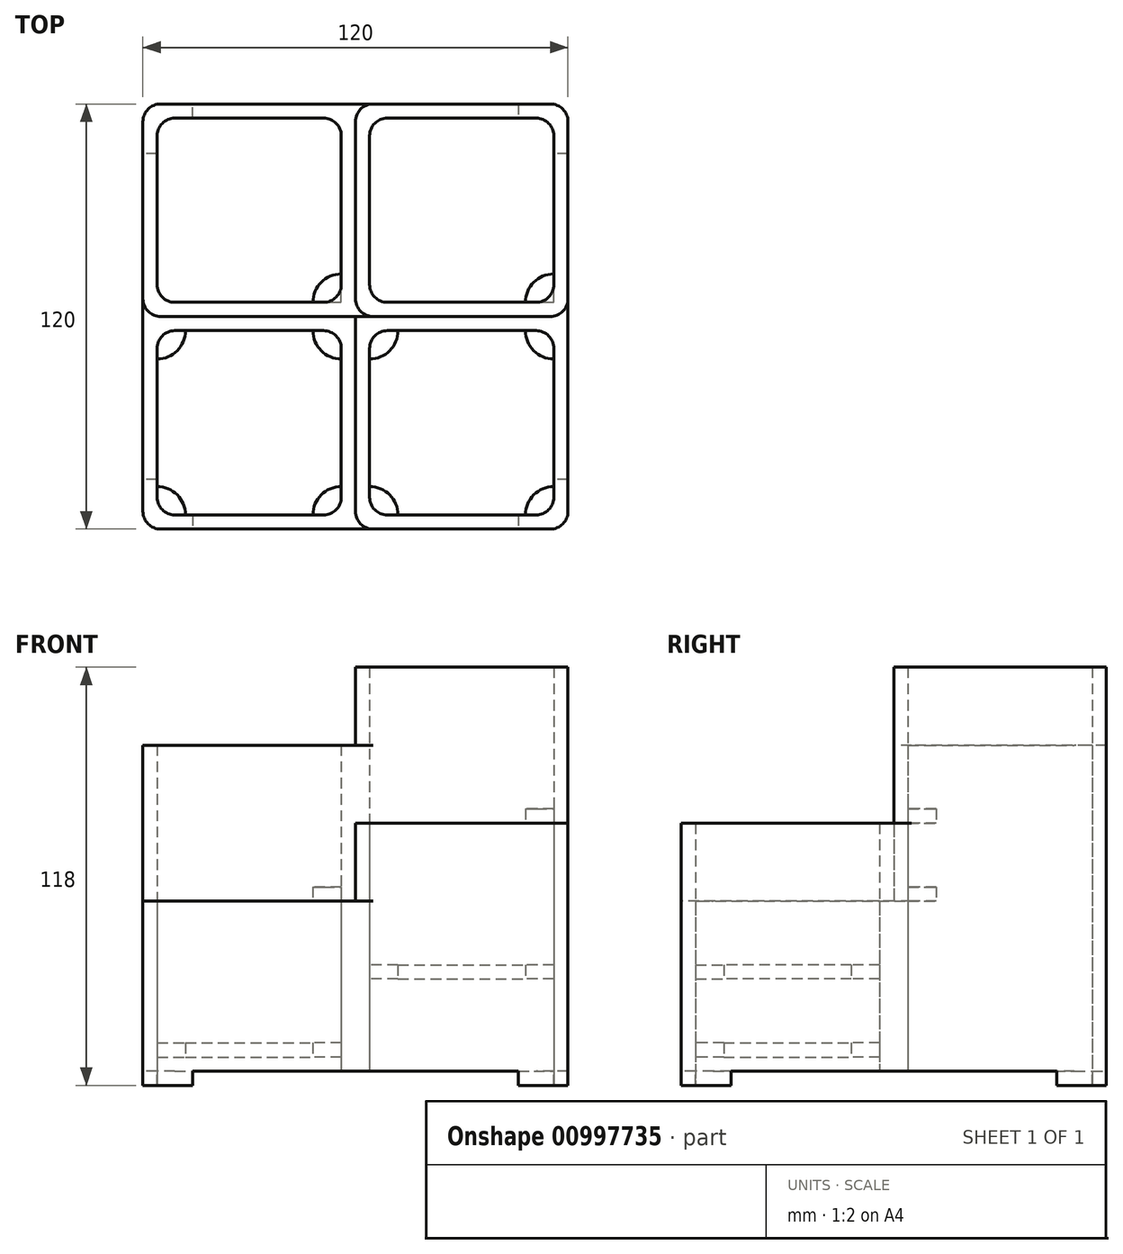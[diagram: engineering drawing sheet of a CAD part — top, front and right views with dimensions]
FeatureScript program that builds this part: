
annotation { "Feature Type Name" : "Feature", "Feature Type Description" : "" }
export const myFeature = defineFeature(function(context is Context, id is Id, definition is map)
    precondition{}
    {
        {
            var Q0;
            Q0=qCreatedBy(makeId("Top.planeOp"),FACE);
            var sketch = newSketch(context, id + "F0", { "sketchPlane" : qUnion([Q0])});
            skLineSegment(sketch, "E0.bottom", {"start": v(60, -60) * mm, "end": v(-60, -60) * mm});
            skLineSegment(sketch, "E0.top", {"start": v(60, 60) * mm, "end": v(-60, 60) * mm});
            skLineSegment(sketch, "E0.left", {"start": v(60, -60) * mm, "end": v(60, 60) * mm});
            skLineSegment(sketch, "E0.right", {"start": v(-60, -60) * mm, "end": v(-60, 60) * mm});
            skPoint(sketch, "E0.middle", {"position": v(0, 0) * mm});
            skLineSegment(sketch, "E1", {"start": v(-56, -16.24) * mm, "end": v(-56, -56) * mm});
            skLineSegment(sketch, "E2", {"start": v(-56, -56) * mm, "end": v(60, -56) * mm});
            skPoint(sketch, "E3.end.orphan", {"position": v(-49.55, -56) * mm});
            skLineSegment(sketch, "E4", {"start": v(-56, -16.24) * mm, "end": v(-56, 60) * mm});
            skLineSegment(sketch, "E5", {"start": v(-35.94, 60) * mm, "end": v(-35.94, 56) * mm});
            skLineSegment(sketch, "E6", {"start": v(60, 22.84) * mm, "end": v(56, 22.84) * mm});
            skLineSegment(sketch, "E7", {"start": v(-56, 56) * mm, "end": v(60, 56) * mm});
            skLineSegment(sketch, "E8", {"start": v(56, -56) * mm, "end": v(56, 56) * mm});
            skLineSegment(sketch, "E9", {"start": v(0, 56) * mm, "end": v(0, -56) * mm});
            skLineSegment(sketch, "E10", {"start": v(56, 0) * mm, "end": v(-56, 0) * mm});
            skLineSegment(sketch, "E11", {"start": v(-4, -56) * mm, "end": v(-4, 56) * mm});
            skLineSegment(sketch, "E12", {"start": v(4, 56) * mm, "end": v(4, -56) * mm});
            skLineSegment(sketch, "E13", {"start": v(-56, 4) * mm, "end": v(56, 4) * mm});
            skLineSegment(sketch, "E14", {"start": v(-56, -4) * mm, "end": v(56, -4) * mm});
            skLineSegment(sketch, "E15", {"start": v(-56, 0) * mm, "end": v(-60, 0) * mm});
            skLineSegment(sketch, "E16", {"start": v(56, 0) * mm, "end": v(60, 0) * mm});
            skLineSegment(sketch, "E17", {"start": v(0, -56) * mm, "end": v(0, -60) * mm});
            skLineSegment(sketch, "E18", {"start": v(0, 56) * mm, "end": v(0, 60) * mm});
            skPoint(sketch, "E19", {"position": v(-46, 56) * mm});
            skLineSegment(sketch, "E20", {"start": v(-46, 56) * mm, "end": v(-46, 60) * mm});
            skLineSegment(sketch, "E21", {"start": v(-56, 56) * mm, "end": v(-60, 56) * mm});
            skLineSegment(sketch, "E22", {"start": v(-56, 46) * mm, "end": v(-60, 46) * mm});
            skLineSegment(sketch, "E23", {"start": v(56, 56) * mm, "end": v(56, 60) * mm});
            skLineSegment(sketch, "E24", {"start": v(46, 60) * mm, "end": v(46, 56) * mm});
            skLineSegment(sketch, "E25", {"start": v(60, 46) * mm, "end": v(56, 46) * mm});
            skLineSegment(sketch, "E26", {"start": v(60, -46) * mm, "end": v(56, -46) * mm});
            skLineSegment(sketch, "E27", {"start": v(56, -56) * mm, "end": v(56, -60) * mm});
            skLineSegment(sketch, "E28", {"start": v(46, -56) * mm, "end": v(46, -60) * mm});
            skLineSegment(sketch, "E29", {"start": v(-56, -56) * mm, "end": v(-56, -60) * mm});
            skLineSegment(sketch, "E30", {"start": v(-56, -56) * mm, "end": v(-60, -56) * mm});
            skLineSegment(sketch, "E31", {"start": v(-46, -56) * mm, "end": v(-46, -60) * mm});
            skLineSegment(sketch, "E32", {"start": v(-56, -46) * mm, "end": v(-60, -46) * mm});
            skArc(sketch, "E33", {"start": v(4, -12) * mm, "mid": v(9.66, -9.66) * mm, "end": v(12, -4) * mm});
            skArc(sketch, "E34", {"start": v(48, -4) * mm, "mid": v(50.34, -9.66) * mm, "end": v(56, -12) * mm});
            skArc(sketch, "E35", {"start": v(56, -48) * mm, "mid": v(50.34, -50.34) * mm, "end": v(48, -56) * mm});
            skArc(sketch, "E36", {"start": v(48, 4) * mm, "mid": v(50.34, 9.66) * mm, "end": v(56, 12) * mm});
            skArc(sketch, "E37", {"start": v(12, 4) * mm, "mid": v(9.66, 9.66) * mm, "end": v(4, 12) * mm});
            skArc(sketch, "E38", {"start": v(-12, -56) * mm, "mid": v(-9.66, -50.34) * mm, "end": v(-4, -48) * mm});
            skArc(sketch, "E39", {"start": v(-4, -12) * mm, "mid": v(-9.66, -9.66) * mm, "end": v(-12, -4) * mm});
            skArc(sketch, "E40", {"start": v(-12, 4) * mm, "mid": v(-9.66, 9.66) * mm, "end": v(-4, 12) * mm});
            skArc(sketch, "E41", {"start": v(-4, 48) * mm, "mid": v(-9.66, 50.34) * mm, "end": v(-12, 56) * mm});
            skArc(sketch, "E42", {"start": v(-48, 56) * mm, "mid": v(-50.34, 50.34) * mm, "end": v(-56, 48) * mm});
            skArc(sketch, "E43", {"start": v(-56, 12) * mm, "mid": v(-50.34, 9.66) * mm, "end": v(-48, 4) * mm});
            skArc(sketch, "E44", {"start": v(-48, -4) * mm, "mid": v(-50.34, -9.66) * mm, "end": v(-56, -12) * mm});
            skArc(sketch, "E45", {"start": v(-56, -48) * mm, "mid": v(-50.34, -50.34) * mm, "end": v(-48, -56) * mm});
            skArc(sketch, "E46", {"start": v(4, -48) * mm, "mid": v(9.66, -50.34) * mm, "end": v(12, -56) * mm});
            skArc(sketch, "E47", {"start": v(48, 56) * mm, "mid": v(50.34, 50.34) * mm, "end": v(56, 48) * mm});
            skArc(sketch, "E48", {"start": v(4, 48) * mm, "mid": v(9.66, 50.34) * mm, "end": v(12, 56) * mm});
            skSolve(sketch);
        }
        {
            var Q0;
            {var subQ0=sQuery(id+"F0.wireOp",EDGE,"E10");var subQ5=sQuery(id+"F0.wireOp",EDGE,"E11");var subQ6=makeQuery(id+"F0.imprint","INTERSECT",VERTEX,{"derivedFrom":[subQ0,subQ5]});Q0=makeQuery(id+"F0.imprint","IMPRINT",FACE,{"disambiguationData":[TD([[makeQuery(id+"F0.imprint","IMPRINT",EDGE,{"disambiguationData":[TD([[subQ6,1.0]])],"derivedFrom":subQ5}),1.0]])]});}
            var Q1;
            {var subQ1=sQuery(id+"F0.wireOp",EDGE,"E1");Q1=makeQuery(id+"F0.imprint","IMPRINT",FACE,{"disambiguationData":[TD([[makeQuery(id+"F0.imprint","IMPRINT",EDGE,{"derivedFrom":subQ1}),-1.0]])]});}
            var Q2;
            {var subQ1=sQuery(id+"F0.wireOp",EDGE,"E2");var subQ3=sQuery(id+"F0.wireOp",EDGE,"E11");var subQ4=makeQuery(id+"F0.imprint","INTERSECT",VERTEX,{"derivedFrom":[subQ1,subQ3]});Q2=makeQuery(id+"F0.imprint","IMPRINT",FACE,{"disambiguationData":[TD([[makeQuery(id+"F0.imprint","IMPRINT",EDGE,{"disambiguationData":[TD([[subQ4,-1.0]])],"derivedFrom":subQ3}),-1.0]])]});}
            var Q3;
            {var subQ0=sQuery(id+"F0.wireOp",EDGE,"E10");var subQ1=sQuery(id+"F0.wireOp",EDGE,"E9");var subQ2=makeQuery(id+"F0.imprint","INTERSECT",VERTEX,{"derivedFrom":[subQ1,subQ0]});Q3=makeQuery(id+"F0.imprint","IMPRINT",FACE,{"disambiguationData":[TD([[makeQuery(id+"F0.imprint","IMPRINT",EDGE,{"disambiguationData":[TD([[subQ2,-1.0]])],"derivedFrom":subQ1}),-1.0]])]});}
            var Q4;
            {var subQ4=sQuery(id+"F0.wireOp",EDGE,"E15");Q4=makeQuery(id+"F0.imprint","IMPRINT",FACE,{"disambiguationData":[TD([[makeQuery(id+"F0.imprint","IMPRINT",EDGE,{"derivedFrom":subQ4}),1.0]])]});}
            var Q5;
            {var subQ0=sQuery(id+"F0.wireOp",EDGE,"E17");Q5=makeQuery(id+"F0.imprint","IMPRINT",FACE,{"disambiguationData":[TD([[makeQuery(id+"F0.imprint","IMPRINT",EDGE,{"derivedFrom":subQ0}),-1.0]])]});}
            var Q6;
            {var subQ0=sQuery(id+"F0.wireOp",EDGE,"E29");Q6=makeQuery(id+"F0.imprint","IMPRINT",FACE,{"disambiguationData":[TD([[makeQuery(id+"F0.imprint","IMPRINT",EDGE,{"derivedFrom":subQ0}),1.0]])]});}
            var Q7;
            {var subQ3=sQuery(id+"F0.wireOp",EDGE,"E29");Q7=makeQuery(id+"F0.imprint","IMPRINT",FACE,{"disambiguationData":[TD([[makeQuery(id+"F0.imprint","IMPRINT",EDGE,{"derivedFrom":subQ3}),-1.0]])]});}
            extrude(context, id + "F1", {"entities" : qUnion([Q0, Q1, Q2, Q3, Q4, Q5, Q6, Q7]), "depth" : 48 * mm, "offsetDistance" : 25 * mm});
        }
        {
            var Q0;
            {var subQ6=sQuery(id+"F0.wireOp",EDGE,"E1");Q0=makeQuery(id+"F0.imprint","IMPRINT",FACE,{"disambiguationData":[TD([[makeQuery(id+"F0.imprint","IMPRINT",EDGE,{"derivedFrom":subQ6}),1.0]])]});}
            extrude(context, id + "F2", {"entities" : qUnion([Q0]), "operationType" : NewBodyOperationType.ADD, "depth" : 8 * mm, "offsetDistance" : 25 * mm});
        }
        {
            var Q0;
            {var subQ1=sQuery(id+"F0.wireOp",EDGE,"E2");var subQ3=sQuery(id+"F0.wireOp",EDGE,"E12");var subQ4=makeQuery(id+"F0.imprint","INTERSECT",VERTEX,{"derivedFrom":[subQ1,subQ3]});Q0=makeQuery(id+"F0.imprint","IMPRINT",FACE,{"disambiguationData":[TD([[makeQuery(id+"F0.imprint","IMPRINT",EDGE,{"disambiguationData":[TD([[subQ4,1.0]])],"derivedFrom":subQ3}),-1.0]])]});}
            var Q1;
            {var subQ0=sQuery(id+"F0.wireOp",EDGE,"E10");var subQ1=sQuery(id+"F0.wireOp",EDGE,"E9");var subQ2=makeQuery(id+"F0.imprint","INTERSECT",VERTEX,{"derivedFrom":[subQ1,subQ0]});Q1=makeQuery(id+"F0.imprint","IMPRINT",FACE,{"disambiguationData":[TD([[makeQuery(id+"F0.imprint","IMPRINT",EDGE,{"disambiguationData":[TD([[subQ2,-1.0]])],"derivedFrom":subQ1}),1.0]])]});}
            var Q2;
            {var subQ0=sQuery(id+"F0.wireOp",EDGE,"E10");var subQ5=sQuery(id+"F0.wireOp",EDGE,"E12");var subQ6=makeQuery(id+"F0.imprint","INTERSECT",VERTEX,{"derivedFrom":[subQ0,subQ5]});Q2=makeQuery(id+"F0.imprint","IMPRINT",FACE,{"disambiguationData":[TD([[makeQuery(id+"F0.imprint","IMPRINT",EDGE,{"disambiguationData":[TD([[subQ6,-1.0]])],"derivedFrom":subQ5}),1.0]])]});}
            var Q3;
            {var subQ0=sQuery(id+"F0.wireOp",EDGE,"E16");Q3=makeQuery(id+"F0.imprint","IMPRINT",FACE,{"disambiguationData":[TD([[makeQuery(id+"F0.imprint","IMPRINT",EDGE,{"derivedFrom":subQ0}),-1.0]])]});}
            var Q4;
            {var subQ7=sQuery(id+"F0.wireOp",EDGE,"E17");Q4=makeQuery(id+"F0.imprint","IMPRINT",FACE,{"disambiguationData":[TD([[makeQuery(id+"F0.imprint","IMPRINT",EDGE,{"derivedFrom":subQ7}),1.0]])]});}
            var Q5;
            {var subQ3=sQuery(id+"F0.wireOp",EDGE,"E26");Q5=makeQuery(id+"F0.imprint","IMPRINT",FACE,{"disambiguationData":[TD([[makeQuery(id+"F0.imprint","IMPRINT",EDGE,{"derivedFrom":subQ3}),1.0]])]});}
            var Q6;
            {var subQ3=sQuery(id+"F0.wireOp",EDGE,"E27");Q6=makeQuery(id+"F0.imprint","IMPRINT",FACE,{"disambiguationData":[TD([[makeQuery(id+"F0.imprint","IMPRINT",EDGE,{"derivedFrom":subQ3}),1.0]])]});}
            var Q7;
            {var subQ0=sQuery(id+"F0.wireOp",EDGE,"E27");Q7=makeQuery(id+"F0.imprint","IMPRINT",FACE,{"disambiguationData":[TD([[makeQuery(id+"F0.imprint","IMPRINT",EDGE,{"derivedFrom":subQ0}),-1.0]])]});}
            extrude(context, id + "F3", {"entities" : qUnion([Q0, Q1, Q2, Q3, Q4, Q5, Q6, Q7]), "operationType" : NewBodyOperationType.ADD, "depth" : 70 * mm, "offsetDistance" : 25 * mm});
        }
        {
            var Q0;
            {var subQ3=sQuery(id+"F0.wireOp",EDGE,"E33");Q0=makeQuery(id+"F0.imprint","IMPRINT",FACE,{"disambiguationData":[TD([[makeQuery(id+"F0.imprint","IMPRINT",EDGE,{"derivedFrom":subQ3}),-1.0]])]});}
            extrude(context, id + "F4", {"entities" : qUnion([Q0]), "operationType" : NewBodyOperationType.ADD, "depth" : 30 * mm, "offsetDistance" : 25 * mm});
        }
        {
            var Q0;
            {var subQ1=sQuery(id+"F0.wireOp",EDGE,"E7");var subQ3=sQuery(id+"F0.wireOp",EDGE,"E12");var subQ4=makeQuery(id+"F0.imprint","INTERSECT",VERTEX,{"derivedFrom":[subQ1,subQ3]});Q0=makeQuery(id+"F0.imprint","IMPRINT",FACE,{"disambiguationData":[TD([[makeQuery(id+"F0.imprint","IMPRINT",EDGE,{"disambiguationData":[TD([[subQ4,-1.0]])],"derivedFrom":subQ3}),-1.0]])]});}
            var Q1;
            {var subQ0=sQuery(id+"F0.wireOp",EDGE,"E18");Q1=makeQuery(id+"F0.imprint","IMPRINT",FACE,{"disambiguationData":[TD([[makeQuery(id+"F0.imprint","IMPRINT",EDGE,{"derivedFrom":subQ0}),-1.0]])]});}
            var Q2;
            {var subQ0=sQuery(id+"F0.wireOp",EDGE,"E6");Q2=makeQuery(id+"F0.imprint","IMPRINT",FACE,{"disambiguationData":[TD([[makeQuery(id+"F0.imprint","IMPRINT",EDGE,{"derivedFrom":subQ0}),-1.0]])]});}
            var Q3;
            {var subQ3=sQuery(id+"F0.wireOp",EDGE,"E6");Q3=makeQuery(id+"F0.imprint","IMPRINT",FACE,{"disambiguationData":[TD([[makeQuery(id+"F0.imprint","IMPRINT",EDGE,{"derivedFrom":subQ3}),1.0]])]});}
            var Q4;
            {var subQ0=sQuery(id+"F0.wireOp",EDGE,"E10");var subQ5=sQuery(id+"F0.wireOp",EDGE,"E12");var subQ6=makeQuery(id+"F0.imprint","INTERSECT",VERTEX,{"derivedFrom":[subQ0,subQ5]});Q4=makeQuery(id+"F0.imprint","IMPRINT",FACE,{"disambiguationData":[TD([[makeQuery(id+"F0.imprint","IMPRINT",EDGE,{"disambiguationData":[TD([[subQ6,1.0]])],"derivedFrom":subQ5}),1.0]])]});}
            var Q5;
            {var subQ0=sQuery(id+"F0.wireOp",EDGE,"E13");var subQ1=sQuery(id+"F0.wireOp",EDGE,"E9");var subQ2=makeQuery(id+"F0.imprint","INTERSECT",VERTEX,{"derivedFrom":[subQ1,subQ0]});Q5=makeQuery(id+"F0.imprint","IMPRINT",FACE,{"disambiguationData":[TD([[makeQuery(id+"F0.imprint","IMPRINT",EDGE,{"disambiguationData":[TD([[subQ2,-1.0]])],"derivedFrom":subQ1}),1.0]])]});}
            var Q6;
            {var subQ0=sQuery(id+"F0.wireOp",EDGE,"E23");Q6=makeQuery(id+"F0.imprint","IMPRINT",FACE,{"disambiguationData":[TD([[makeQuery(id+"F0.imprint","IMPRINT",EDGE,{"derivedFrom":subQ0}),1.0]])]});}
            var Q7;
            {var subQ3=sQuery(id+"F0.wireOp",EDGE,"E23");Q7=makeQuery(id+"F0.imprint","IMPRINT",FACE,{"disambiguationData":[TD([[makeQuery(id+"F0.imprint","IMPRINT",EDGE,{"derivedFrom":subQ3}),-1.0]])]});}
            var Q8;
            {var subQ3=sQuery(id+"F0.wireOp",EDGE,"E25");Q8=makeQuery(id+"F0.imprint","IMPRINT",FACE,{"disambiguationData":[TD([[makeQuery(id+"F0.imprint","IMPRINT",EDGE,{"derivedFrom":subQ3}),-1.0]])]});}
            extrude(context, id + "F5", {"entities" : qUnion([Q0, Q1, Q2, Q3, Q4, Q5, Q6, Q7, Q8]), "operationType" : NewBodyOperationType.ADD, "depth" : 114 * mm, "offsetDistance" : 25 * mm});
        }
        {
            var Q0;
            {var subQ1=sQuery(id+"F0.wireOp",EDGE,"E36");Q0=makeQuery(id+"F0.imprint","IMPRINT",FACE,{"disambiguationData":[TD([[makeQuery(id+"F0.imprint","IMPRINT",EDGE,{"derivedFrom":subQ1}),1.0]])]});}
            extrude(context, id + "F6", {"entities" : qUnion([Q0]), "operationType" : NewBodyOperationType.ADD, "depth" : 74 * mm, "offsetDistance" : 25 * mm});
        }
        {
            var Q0;
            {var subQ0=sQuery(id+"F0.wireOp",EDGE,"E10");var subQ5=sQuery(id+"F0.wireOp",EDGE,"E11");var subQ6=makeQuery(id+"F0.imprint","INTERSECT",VERTEX,{"derivedFrom":[subQ0,subQ5]});Q0=makeQuery(id+"F0.imprint","IMPRINT",FACE,{"disambiguationData":[TD([[makeQuery(id+"F0.imprint","IMPRINT",EDGE,{"disambiguationData":[TD([[subQ6,-1.0]])],"derivedFrom":subQ5}),1.0]])]});}
            var Q1;
            {var subQ1=sQuery(id+"F0.wireOp",EDGE,"E7");var subQ3=sQuery(id+"F0.wireOp",EDGE,"E11");var subQ4=makeQuery(id+"F0.imprint","INTERSECT",VERTEX,{"derivedFrom":[subQ1,subQ3]});Q1=makeQuery(id+"F0.imprint","IMPRINT",FACE,{"disambiguationData":[TD([[makeQuery(id+"F0.imprint","IMPRINT",EDGE,{"disambiguationData":[TD([[subQ4,1.0]])],"derivedFrom":subQ3}),-1.0]])]});}
            var Q2;
            {var subQ0=sQuery(id+"F0.wireOp",EDGE,"E13");var subQ1=sQuery(id+"F0.wireOp",EDGE,"E9");var subQ2=makeQuery(id+"F0.imprint","INTERSECT",VERTEX,{"derivedFrom":[subQ1,subQ0]});Q2=makeQuery(id+"F0.imprint","IMPRINT",FACE,{"disambiguationData":[TD([[makeQuery(id+"F0.imprint","IMPRINT",EDGE,{"disambiguationData":[TD([[subQ2,-1.0]])],"derivedFrom":subQ1}),-1.0]])]});}
            var Q3;
            {var subQ1=sQuery(id+"F0.wireOp",EDGE,"E5");Q3=makeQuery(id+"F0.imprint","IMPRINT",FACE,{"disambiguationData":[TD([[makeQuery(id+"F0.imprint","IMPRINT",EDGE,{"derivedFrom":subQ1}),1.0]])]});}
            var Q4;
            {var subQ3=sQuery(id+"F0.wireOp",EDGE,"E5");Q4=makeQuery(id+"F0.imprint","IMPRINT",FACE,{"disambiguationData":[TD([[makeQuery(id+"F0.imprint","IMPRINT",EDGE,{"derivedFrom":subQ3}),-1.0]])]});}
            var Q5;
            {var subQ0=sQuery(id+"F0.wireOp",EDGE,"E15");Q5=makeQuery(id+"F0.imprint","IMPRINT",FACE,{"disambiguationData":[TD([[makeQuery(id+"F0.imprint","IMPRINT",EDGE,{"derivedFrom":subQ0}),-1.0]])]});}
            var Q6;
            {var subQ3=sQuery(id+"F0.wireOp",EDGE,"E20");Q6=makeQuery(id+"F0.imprint","IMPRINT",FACE,{"disambiguationData":[TD([[makeQuery(id+"F0.imprint","IMPRINT",EDGE,{"derivedFrom":subQ3}),1.0]])]});}
            var Q7;
            {var subQ5=sQuery(id+"F0.wireOp",EDGE,"E21");Q7=makeQuery(id+"F0.imprint","IMPRINT",FACE,{"disambiguationData":[TD([[makeQuery(id+"F0.imprint","IMPRINT",EDGE,{"derivedFrom":subQ5}),-1.0]])]});}
            var Q8;
            {var subQ0=sQuery(id+"F0.wireOp",EDGE,"E21");Q8=makeQuery(id+"F0.imprint","IMPRINT",FACE,{"disambiguationData":[TD([[makeQuery(id+"F0.imprint","IMPRINT",EDGE,{"derivedFrom":subQ0}),1.0]])]});}
            extrude(context, id + "F7", {"entities" : qUnion([Q0, Q1, Q2, Q3, Q4, Q5, Q6, Q7, Q8]), "operationType" : NewBodyOperationType.ADD, "depth" : 92 * mm, "offsetDistance" : 25 * mm});
        }
        {
            var Q0;
            {var subQ1=sQuery(id+"F0.wireOp",EDGE,"E40");Q0=makeQuery(id+"F0.imprint","IMPRINT",FACE,{"disambiguationData":[TD([[makeQuery(id+"F0.imprint","IMPRINT",EDGE,{"derivedFrom":subQ1}),1.0]])]});}
            extrude(context, id + "F8", {"entities" : qUnion([Q0]), "operationType" : NewBodyOperationType.ADD, "depth" : 52 * mm, "offsetDistance" : 25 * mm});
        }
        {
            var Q0;
            {var subQ6=sQuery(id+"F0.wireOp",EDGE,"E1");Q0=makeQuery(id+"F0.imprint","IMPRINT",FACE,{"disambiguationData":[TD([[makeQuery(id+"F0.imprint","IMPRINT",EDGE,{"derivedFrom":subQ6}),1.0]])]});}
            extrude(context, id + "F9", {"entities" : qUnion([Q0]), "operationType" : NewBodyOperationType.REMOVE, "depth" : 4 * mm, "offsetDistance" : 25 * mm});
        }
        {
            var Q0;
            {var subQ1=sQuery(id+"F0.wireOp",EDGE,"E40");Q0=makeQuery(id+"F0.imprint","IMPRINT",FACE,{"disambiguationData":[TD([[makeQuery(id+"F0.imprint","IMPRINT",EDGE,{"derivedFrom":subQ1}),1.0]])]});}
            extrude(context, id + "F10", {"entities" : qUnion([Q0]), "operationType" : NewBodyOperationType.REMOVE, "depth" : 48 * mm, "offsetDistance" : 25 * mm});
        }
        {
            var Q0;
            {var subQ3=sQuery(id+"F0.wireOp",EDGE,"E33");Q0=makeQuery(id+"F0.imprint","IMPRINT",FACE,{"disambiguationData":[TD([[makeQuery(id+"F0.imprint","IMPRINT",EDGE,{"derivedFrom":subQ3}),-1.0]])]});}
            extrude(context, id + "F11", {"entities" : qUnion([Q0]), "operationType" : NewBodyOperationType.REMOVE, "depth" : 26 * mm, "offsetDistance" : 25 * mm});
        }
        {
            var Q0;
            {var subQ1=sQuery(id+"F0.wireOp",EDGE,"E36");Q0=makeQuery(id+"F0.imprint","IMPRINT",FACE,{"disambiguationData":[TD([[makeQuery(id+"F0.imprint","IMPRINT",EDGE,{"derivedFrom":subQ1}),1.0]])]});}
            extrude(context, id + "F12", {"entities" : qUnion([Q0]), "operationType" : NewBodyOperationType.REMOVE, "depth" : 70 * mm, "offsetDistance" : 25 * mm});
        }
        {
            var Q0;
            {var subQ3=sQuery(id+"F0.wireOp",EDGE,"E20");Q0=makeQuery(id+"F0.imprint","IMPRINT",FACE,{"disambiguationData":[TD([[makeQuery(id+"F0.imprint","IMPRINT",EDGE,{"derivedFrom":subQ3}),1.0]])]});}
            var Q1;
            {var subQ5=sQuery(id+"F0.wireOp",EDGE,"E21");Q1=makeQuery(id+"F0.imprint","IMPRINT",FACE,{"disambiguationData":[TD([[makeQuery(id+"F0.imprint","IMPRINT",EDGE,{"derivedFrom":subQ5}),-1.0]])]});}
            var Q2;
            {var subQ0=sQuery(id+"F0.wireOp",EDGE,"E21");Q2=makeQuery(id+"F0.imprint","IMPRINT",FACE,{"disambiguationData":[TD([[makeQuery(id+"F0.imprint","IMPRINT",EDGE,{"derivedFrom":subQ0}),1.0]])]});}
            var Q3;
            {var subQ0=sQuery(id+"F0.wireOp",EDGE,"E23");Q3=makeQuery(id+"F0.imprint","IMPRINT",FACE,{"disambiguationData":[TD([[makeQuery(id+"F0.imprint","IMPRINT",EDGE,{"derivedFrom":subQ0}),1.0]])]});}
            var Q4;
            {var subQ3=sQuery(id+"F0.wireOp",EDGE,"E23");Q4=makeQuery(id+"F0.imprint","IMPRINT",FACE,{"disambiguationData":[TD([[makeQuery(id+"F0.imprint","IMPRINT",EDGE,{"derivedFrom":subQ3}),-1.0]])]});}
            var Q5;
            {var subQ3=sQuery(id+"F0.wireOp",EDGE,"E25");Q5=makeQuery(id+"F0.imprint","IMPRINT",FACE,{"disambiguationData":[TD([[makeQuery(id+"F0.imprint","IMPRINT",EDGE,{"derivedFrom":subQ3}),-1.0]])]});}
            var Q6;
            {var subQ3=sQuery(id+"F0.wireOp",EDGE,"E26");Q6=makeQuery(id+"F0.imprint","IMPRINT",FACE,{"disambiguationData":[TD([[makeQuery(id+"F0.imprint","IMPRINT",EDGE,{"derivedFrom":subQ3}),1.0]])]});}
            var Q7;
            {var subQ0=sQuery(id+"F0.wireOp",EDGE,"E27");Q7=makeQuery(id+"F0.imprint","IMPRINT",FACE,{"disambiguationData":[TD([[makeQuery(id+"F0.imprint","IMPRINT",EDGE,{"derivedFrom":subQ0}),-1.0]])]});}
            var Q8;
            {var subQ3=sQuery(id+"F0.wireOp",EDGE,"E27");Q8=makeQuery(id+"F0.imprint","IMPRINT",FACE,{"disambiguationData":[TD([[makeQuery(id+"F0.imprint","IMPRINT",EDGE,{"derivedFrom":subQ3}),1.0]])]});}
            var Q9;
            {var subQ0=sQuery(id+"F0.wireOp",EDGE,"E30");Q9=makeQuery(id+"F0.imprint","IMPRINT",FACE,{"disambiguationData":[TD([[makeQuery(id+"F0.imprint","IMPRINT",EDGE,{"derivedFrom":subQ0}),-1.0]])]});}
            var Q10;
            {var subQ3=sQuery(id+"F0.wireOp",EDGE,"E29");Q10=makeQuery(id+"F0.imprint","IMPRINT",FACE,{"disambiguationData":[TD([[makeQuery(id+"F0.imprint","IMPRINT",EDGE,{"derivedFrom":subQ3}),-1.0]])]});}
            var Q11;
            {var subQ0=sQuery(id+"F0.wireOp",EDGE,"E29");Q11=makeQuery(id+"F0.imprint","IMPRINT",FACE,{"disambiguationData":[TD([[makeQuery(id+"F0.imprint","IMPRINT",EDGE,{"derivedFrom":subQ0}),1.0]])]});}
            extrude(context, id + "F13", {"entities" : qUnion([Q0, Q1, Q2, Q3, Q4, Q5, Q6, Q7, Q8, Q9, Q10, Q11]), "operationType" : NewBodyOperationType.ADD, "oppositeDirection" : true, "depth" : 4 * mm, "offsetDistance" : 25 * mm});
        }
        {
            var Q0;
            Q0=makeQuery(id+"F7.opExtrude","SWEPT_EDGE",EDGE,{"disambiguationData":[OSD([sQuery(id+"F0.wireOp",EDGE,"E0.top"),sQuery(id+"F0.wireOp",EDGE,"E0.right")])]});
            var Q1;
            Q1=makeQuery(id+"F7.opExtrude","SWEPT_EDGE",EDGE,{"disambiguationData":[OSD([sQuery(id+"F0.wireOp",EDGE,"E0.right"),sQuery(id+"F0.wireOp",EDGE,"E15")])]});
            var Q2;
            Q2=makeQuery(id+"F1.opExtrude","SWEPT_EDGE",EDGE,{"disambiguationData":[OSD([sQuery(id+"F0.wireOp",EDGE,"E0.bottom"),sQuery(id+"F0.wireOp",EDGE,"E0.right")])]});
            var Q3;
            Q3=makeQuery(id+"F3.opExtrude","SWEPT_EDGE",EDGE,{"disambiguationData":[OSD([sQuery(id+"F0.wireOp",EDGE,"E0.bottom"),sQuery(id+"F0.wireOp",EDGE,"E0.left")])]});
            var Q4;
            Q4=makeQuery(id+"F3.opExtrude","SWEPT_EDGE",EDGE,{"disambiguationData":[OSD([sQuery(id+"F0.wireOp",EDGE,"E0.bottom"),sQuery(id+"F0.wireOp",EDGE,"E17")])]});
            var Q5;
            Q5=makeQuery(id+"F5.opExtrude","SWEPT_EDGE",EDGE,{"disambiguationData":[OSD([sQuery(id+"F0.wireOp",EDGE,"E0.top"),sQuery(id+"F0.wireOp",EDGE,"E0.left")])]});
            var Q6;
            Q6=makeQuery(id+"F5.opExtrude","SWEPT_EDGE",EDGE,{"disambiguationData":[OSD([sQuery(id+"F0.wireOp",EDGE,"E0.top"),sQuery(id+"F0.wireOp",EDGE,"E18")])]});
            var Q7;
            {var subQ0=sQuery(id+"F0.wireOp",EDGE,"E9");var subQ1=sQuery(id+"F0.wireOp",EDGE,"E10");Q7=makeQuery(id+"F5.boolean.opBoolean","SPLIT",EDGE,{"disambiguationData":[topologyDisambiguationEdgeConnected([makeQuery(id+"F5.opExtrude","SWEPT_FACE",FACE,{"disambiguationData":[OSD([subQ1,sQuery(id+"F0.wireOp",EDGE,"E16")])]})])],"derivedFrom":makeQuery(id+"F5.opExtrude","SWEPT_EDGE",EDGE,{"disambiguationData":[OSD([subQ0,subQ1])]})});}
            var Q8;
            Q8=makeQuery(id+"F5.opExtrude","SWEPT_EDGE",EDGE,{"disambiguationData":[OSD([sQuery(id+"F0.wireOp",EDGE,"E0.left"),sQuery(id+"F0.wireOp",EDGE,"E16")])]});
            var Q9;
            Q9=makeQuery(id+"F7.opExtrude","SWEPT_EDGE",EDGE,{"disambiguationData":[OSD([sQuery(id+"F0.wireOp",EDGE,"E7"),sQuery(id+"F0.wireOp",EDGE,"E11")])]});
            var Q10;
            Q10=makeQuery(id+"F7.opExtrude","SWEPT_EDGE",EDGE,{"disambiguationData":[OSD([sQuery(id+"F0.wireOp",EDGE,"E11"),sQuery(id+"F0.wireOp",EDGE,"E13")])]});
            var Q11;
            Q11=makeQuery(id+"F7.opExtrude","SWEPT_EDGE",EDGE,{"disambiguationData":[OSD([sQuery(id+"F0.wireOp",EDGE,"E4"),sQuery(id+"F0.wireOp",EDGE,"E7")])]});
            var Q12;
            Q12=makeQuery(id+"F7.opExtrude","SWEPT_EDGE",EDGE,{"disambiguationData":[OSD([sQuery(id+"F0.wireOp",EDGE,"E4"),sQuery(id+"F0.wireOp",EDGE,"E13")])]});
            var Q13;
            Q13=makeQuery(id+"F1.opExtrude","SWEPT_EDGE",EDGE,{"disambiguationData":[OSD([sQuery(id+"F0.wireOp",EDGE,"E4"),sQuery(id+"F0.wireOp",EDGE,"E14")])]});
            var Q14;
            Q14=makeQuery(id+"F1.opExtrude","SWEPT_EDGE",EDGE,{"disambiguationData":[OSD([sQuery(id+"F0.wireOp",EDGE,"E11"),sQuery(id+"F0.wireOp",EDGE,"E14")])]});
            var Q15;
            Q15=makeQuery(id+"F1.opExtrude","SWEPT_EDGE",EDGE,{"disambiguationData":[OSD([sQuery(id+"F0.wireOp",EDGE,"E2"),sQuery(id+"F0.wireOp",EDGE,"E11")])]});
            var Q16;
            Q16=makeQuery(id+"F1.opExtrude","SWEPT_EDGE",EDGE,{"disambiguationData":[OSD([sQuery(id+"F0.wireOp",EDGE,"E1"),sQuery(id+"F0.wireOp",EDGE,"E2")])]});
            var Q17;
            Q17=makeQuery(id+"F3.opExtrude","SWEPT_EDGE",EDGE,{"disambiguationData":[OSD([sQuery(id+"F0.wireOp",EDGE,"E2"),sQuery(id+"F0.wireOp",EDGE,"E12")])]});
            var Q18;
            Q18=makeQuery(id+"F3.opExtrude","SWEPT_EDGE",EDGE,{"disambiguationData":[OSD([sQuery(id+"F0.wireOp",EDGE,"E12"),sQuery(id+"F0.wireOp",EDGE,"E14")])]});
            var Q19;
            Q19=makeQuery(id+"F3.opExtrude","SWEPT_EDGE",EDGE,{"disambiguationData":[OSD([sQuery(id+"F0.wireOp",EDGE,"E8"),sQuery(id+"F0.wireOp",EDGE,"E14")])]});
            var Q20;
            Q20=makeQuery(id+"F3.opExtrude","SWEPT_EDGE",EDGE,{"disambiguationData":[OSD([sQuery(id+"F0.wireOp",EDGE,"E2"),sQuery(id+"F0.wireOp",EDGE,"E8")])]});
            var Q21;
            Q21=makeQuery(id+"F5.opExtrude","SWEPT_EDGE",EDGE,{"disambiguationData":[OSD([sQuery(id+"F0.wireOp",EDGE,"E8"),sQuery(id+"F0.wireOp",EDGE,"E13")])]});
            var Q22;
            Q22=makeQuery(id+"F5.opExtrude","SWEPT_EDGE",EDGE,{"disambiguationData":[OSD([sQuery(id+"F0.wireOp",EDGE,"E7"),sQuery(id+"F0.wireOp",EDGE,"E8")])]});
            var Q23;
            Q23=makeQuery(id+"F5.opExtrude","SWEPT_EDGE",EDGE,{"disambiguationData":[OSD([sQuery(id+"F0.wireOp",EDGE,"E7"),sQuery(id+"F0.wireOp",EDGE,"E12")])]});
            var Q24;
            Q24=makeQuery(id+"F5.opExtrude","SWEPT_EDGE",EDGE,{"disambiguationData":[OSD([sQuery(id+"F0.wireOp",EDGE,"E12"),sQuery(id+"F0.wireOp",EDGE,"E13")])]});
            fillet(context, id + "F14", {"entities" : qUnion([Q0, Q1, Q2, Q3, Q4, Q5, Q6, Q7, Q8, Q9, Q10, Q11, Q12, Q13, Q14, Q15, Q16, Q17, Q18, Q19, Q20, Q21, Q22, Q23, Q24]), "radius" : 5 * mm, "tangentPropagation" : true, "allowEdgeOverflow" : false});
        }
    });
